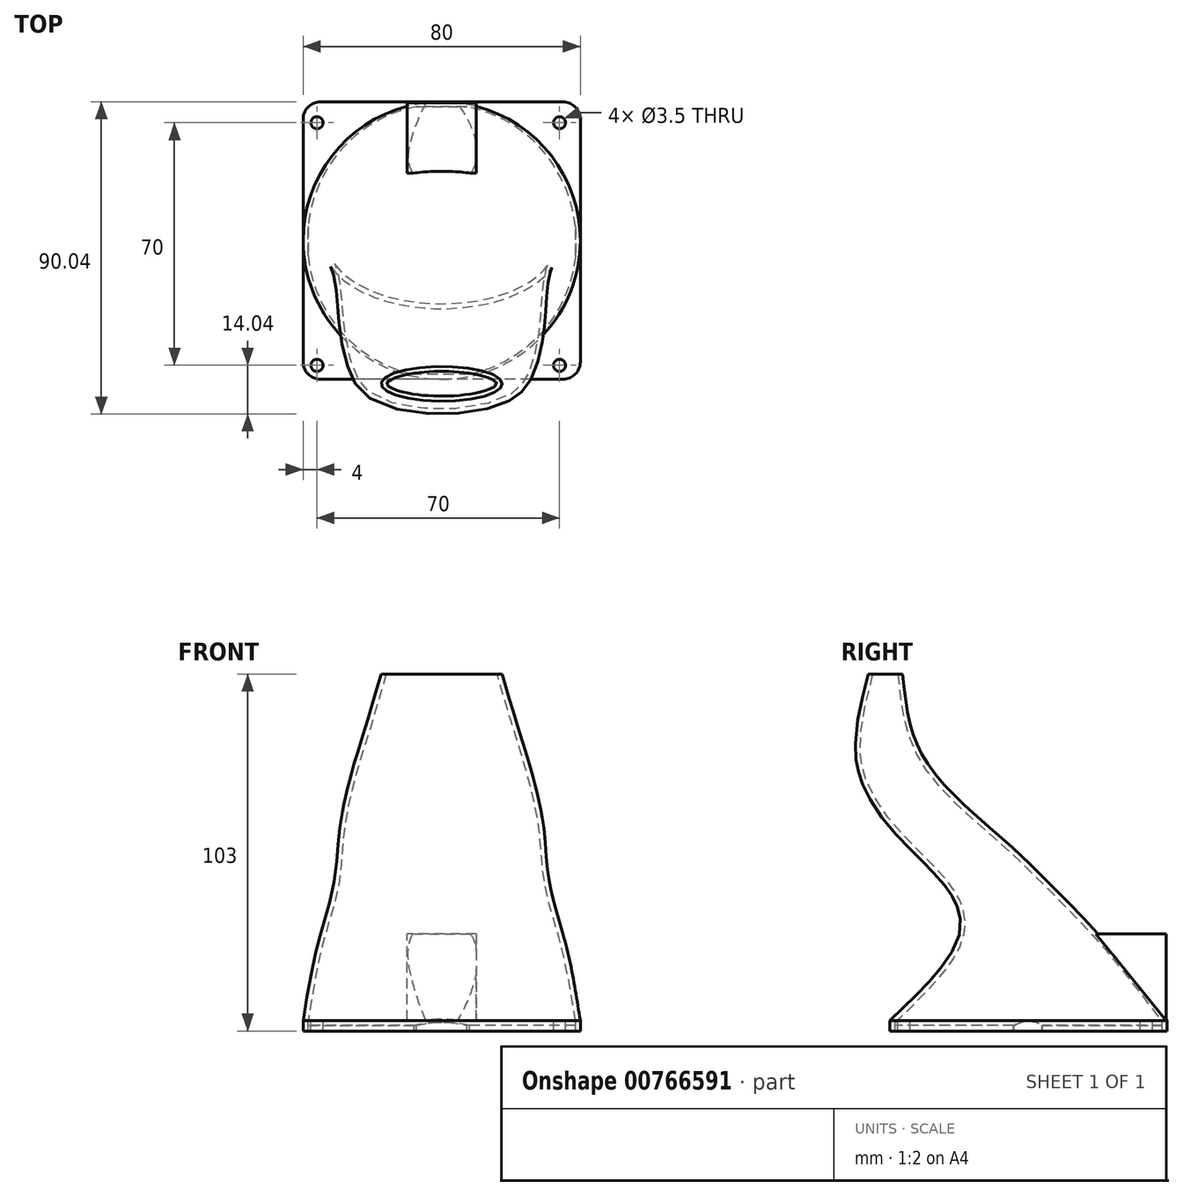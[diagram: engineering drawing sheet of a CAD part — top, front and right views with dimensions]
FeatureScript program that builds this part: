
annotation { "Feature Type Name" : "Feature", "Feature Type Description" : "" }
export const myFeature = defineFeature(function(context is Context, id is Id, definition is map)
    precondition{}
    {
        {
            var Q0;
            Q0=qCreatedBy(makeId("Top.planeOp"),FACE);
            var sketch = newSketch(context, id + "F0", { "sketchPlane" : qUnion([Q0])});
            skEllipse(sketch, "E0", {"center": v(0, 0) * mm, "majorRadius": 35 * mm, "minorRadius": 20 * mm, "majorAxis": v(1, 0)});
            skSolve(sketch);
        }
        {
            var Q0;
            Q0=qCreatedBy(makeId("Top.planeOp"),FACE);
            cPlane(context, id + "F1", {"entities" : qUnion([Q0]), "cplaneType" : CPlaneType.OFFSET, "offset" : 25 * mm, "oppositeDirection" : true, "width" : 150 * mm, "height" : 150 * mm});
        }
        {
            var Q0;
            Q0=qCreatedBy(id+"F1.planeOp",FACE);
            var sketch = newSketch(context, id + "F2", { "sketchPlane" : qUnion([Q0])});
            skCircle(sketch, "E1", {"center": v(0, 0) * mm, "radius": 40 * mm});
            skSolve(sketch);
        }
        {
            var Q0;
            Q0=qCreatedBy(makeId("Top.planeOp"),FACE);
            cPlane(context, id + "F3", {"entities" : qUnion([Q0]), "cplaneType" : CPlaneType.OFFSET, "offset" : 25 * mm, "width" : 150 * mm, "height" : 150 * mm});
        }
        {
            var Q0;
            Q0=qCreatedBy(id+"F3.planeOp",FACE);
            var sketch = newSketch(context, id + "F4", { "sketchPlane" : qUnion([Q0])});
            skEllipse(sketch, "E2", {"center": v(0, -19.77) * mm, "majorRadius": 30 * mm, "minorRadius": 15 * mm, "majorAxis": v(1, 0)});
            skSolve(sketch);
        }
        {
            var Q0;
            Q0=qCreatedBy(id+"F3.planeOp",FACE);
            cPlane(context, id + "F5", {"entities" : qUnion([Q0]), "cplaneType" : CPlaneType.OFFSET, "offset" : 25 * mm, "width" : 150 * mm, "height" : 150 * mm});
        }
        {
            var Q0;
            Q0=qCreatedBy(id+"F5.planeOp",FACE);
            var sketch = newSketch(context, id + "F6", { "sketchPlane" : qUnion([Q0])});
            skEllipse(sketch, "E3", {"center": v(0, -39.76) * mm, "majorRadius": 25 * mm, "minorRadius": 10 * mm, "majorAxis": v(1, 0)});
            skSolve(sketch);
        }
        {
            var Q0;
            Q0=qCreatedBy(id+"F5.planeOp",FACE);
            cPlane(context, id + "F7", {"entities" : qUnion([Q0]), "cplaneType" : CPlaneType.OFFSET, "offset" : 25 * mm, "width" : 150 * mm, "height" : 150 * mm});
        }
        {
            var Q0;
            Q0=qCreatedBy(id+"F7.planeOp",FACE);
            var sketch = newSketch(context, id + "F8", { "sketchPlane" : qUnion([Q0])});
            skEllipse(sketch, "E4", {"center": v(0, -41.33) * mm, "majorRadius": 17.5 * mm, "minorRadius": 5 * mm, "majorAxis": v(1, 0)});
            skSolve(sketch);
        }
        {
            var Q0;
            Q0=makeQuery(id+"F2.imprint","IMPRINT",FACE,{"disambiguationData":[TD([[makeQuery(id+"F2.imprint","IMPRINT",EDGE,{"derivedFrom":sQuery(id+"F2.wireOp",EDGE,"E1")}),1.0]])]});
            var Q1;
            Q1=makeQuery(id+"F0.imprint","IMPRINT",FACE,{"disambiguationData":[TD([[makeQuery(id+"F0.imprint","IMPRINT",EDGE,{"derivedFrom":sQuery(id+"F0.wireOp",EDGE,"E0")}),1.0]])]});
            var Q2;
            Q2=makeQuery(id+"F4.imprint","IMPRINT",FACE,{"disambiguationData":[TD([[makeQuery(id+"F4.imprint","IMPRINT",EDGE,{"derivedFrom":sQuery(id+"F4.wireOp",EDGE,"E2")}),1.0]])]});
            var Q3;
            Q3=makeQuery(id+"F6.imprint","IMPRINT",FACE,{"disambiguationData":[TD([[makeQuery(id+"F6.imprint","IMPRINT",EDGE,{"derivedFrom":sQuery(id+"F6.wireOp",EDGE,"E3")}),1.0]])]});
            var Q4;
            Q4=makeQuery(id+"F8.imprint","IMPRINT",FACE,{"disambiguationData":[TD([[makeQuery(id+"F8.imprint","IMPRINT",EDGE,{"derivedFrom":sQuery(id+"F8.wireOp",EDGE,"E4")}),1.0]])]});
            loft(context, id + "F9", {"sheetProfilesArray" : [{ "sheetProfileEntities" : qUnion([Q0]) }, { "sheetProfileEntities" : qUnion([Q1]) }, { "sheetProfileEntities" : qUnion([Q2]) }, { "sheetProfileEntities" : qUnion([Q3]) }, { "sheetProfileEntities" : qUnion([Q4]) }]});
        }
        {
            var Q0;
            Q0=makeQuery(id+"F9.opLoft","CAP_FACE",FACE,{"disambiguationData":[OSD([makeQuery(id+"F2.imprint","IMPRINT",FACE,{"disambiguationData":[TD([[makeQuery(id+"F2.imprint","IMPRINT",EDGE,{"derivedFrom":sQuery(id+"F2.wireOp",EDGE,"E1")}),1.0]])]})])],"isStart":true});
            var sketch = newSketch(context, id + "F10", { "sketchPlane" : qUnion([Q0])});
            skLineSegment(sketch, "E5.bottom", {"start": v(40, -40) * mm, "end": v(-40, -40) * mm});
            skLineSegment(sketch, "E5.top", {"start": v(40, 40) * mm, "end": v(-40, 40) * mm});
            skLineSegment(sketch, "E5.left", {"start": v(40, -40) * mm, "end": v(40, 40) * mm});
            skLineSegment(sketch, "E5.right", {"start": v(-40, -40) * mm, "end": v(-40, 40) * mm});
            skCircle(sketch, "E6", {"center": v(34, -34) * mm, "radius": 1.75 * mm});
            skCircle(sketch, "E7.0.1.0", {"center": v(34, 36) * mm, "radius": 1.75 * mm});
            skCircle(sketch, "E7.1.0.0", {"center": v(-36, -34) * mm, "radius": 1.75 * mm});
            skCircle(sketch, "E7.1.1.0", {"center": v(-36, 36) * mm, "radius": 1.75 * mm});
            skLineSegment(sketch, "E7.direction1", {"start": v(34, -34) * mm, "end": v(-36, -34) * mm, "construction": true});
            skLineSegment(sketch, "E7.direction2", {"start": v(34, -34) * mm, "end": v(34, 36) * mm, "construction": true});
            skSolve(sketch);
        }
        {
            var Q0;
            {var subQ0=sQuery(id+"F10.wireOp",EDGE,"E5.left");var subQ1=sQuery(id+"F10.wireOp",EDGE,"E5.bottom");var subQ2=makeQuery(id+"F10.imprint","INTERSECT",VERTEX,{"derivedFrom":[subQ1,subQ0]});Q0=makeQuery(id+"F10.imprint","IMPRINT",FACE,{"disambiguationData":[TD([[makeQuery(id+"F10.imprint","IMPRINT",EDGE,{"disambiguationData":[TD([[subQ2,-1.0]])],"derivedFrom":subQ1}),-1.0]])]});}
            var Q1;
            {var subQ0=makeQuery(id+"F9.opLoft","MID_CAP_EDGE",EDGE,{"disambiguationData":[OSD([sQuery(id+"F2.wireOp",EDGE,"E1")])],"capPos":0.0});var subQ1=makeQuery(id+"F10.imprint","INTERSECT",VERTEX,{"derivedFrom":[subQ0,sQuery(id+"F10.wireOp",EDGE,"E5.bottom")]});Q1=makeQuery(id+"F10.imprint","IMPRINT",FACE,{"disambiguationData":[TD([[makeQuery(id+"F10.imprint","IMPRINT",EDGE,{"disambiguationData":[TD([[subQ1,-1.0]])],"derivedFrom":subQ0}),1.0]])]});}
            var Q2;
            {var subQ0=sQuery(id+"F10.wireOp",EDGE,"E5.right");var subQ1=sQuery(id+"F10.wireOp",EDGE,"E5.bottom");var subQ2=makeQuery(id+"F10.imprint","INTERSECT",VERTEX,{"derivedFrom":[subQ1,subQ0]});Q2=makeQuery(id+"F10.imprint","IMPRINT",FACE,{"disambiguationData":[TD([[makeQuery(id+"F10.imprint","IMPRINT",EDGE,{"disambiguationData":[TD([[subQ2,1.0]])],"derivedFrom":subQ1}),-1.0]])]});}
            var Q3;
            {var subQ0=sQuery(id+"F10.wireOp",EDGE,"E5.right");var subQ1=sQuery(id+"F10.wireOp",EDGE,"E5.top");var subQ2=makeQuery(id+"F10.imprint","INTERSECT",VERTEX,{"derivedFrom":[subQ1,subQ0]});Q3=makeQuery(id+"F10.imprint","IMPRINT",FACE,{"disambiguationData":[TD([[makeQuery(id+"F10.imprint","IMPRINT",EDGE,{"disambiguationData":[TD([[subQ2,1.0]])],"derivedFrom":subQ1}),1.0]])]});}
            var Q4;
            {var subQ0=sQuery(id+"F10.wireOp",EDGE,"E5.left");var subQ1=sQuery(id+"F10.wireOp",EDGE,"E5.top");var subQ2=makeQuery(id+"F10.imprint","INTERSECT",VERTEX,{"derivedFrom":[subQ1,subQ0]});Q4=makeQuery(id+"F10.imprint","IMPRINT",FACE,{"disambiguationData":[TD([[makeQuery(id+"F10.imprint","IMPRINT",EDGE,{"disambiguationData":[TD([[subQ2,-1.0]])],"derivedFrom":subQ1}),1.0]])]});}
            extrude(context, id + "F11", {"entities" : qUnion([Q0, Q1, Q2, Q3, Q4]), "operationType" : NewBodyOperationType.ADD, "depth" : 3 * mm, "offsetDistance" : 25 * mm});
        }
        {
            var Q0;
            Q0=makeQuery(id+"F9.opLoft","CAP_FACE",FACE,{"disambiguationData":[OSD([makeQuery(id+"F8.imprint","IMPRINT",FACE,{"disambiguationData":[TD([[makeQuery(id+"F8.imprint","IMPRINT",EDGE,{"derivedFrom":sQuery(id+"F8.wireOp",EDGE,"E4")}),1.0]])]})])],"isStart":true});
            var Q1;
            Q1=makeQuery(id+"F11.opExtrude","CAP_FACE",FACE,{"disambiguationData":[OSD([sQuery(id+"F10.wireOp",EDGE,"E5.bottom"),sQuery(id+"F10.wireOp",EDGE,"E5.top"),sQuery(id+"F10.wireOp",EDGE,"E5.left"),sQuery(id+"F10.wireOp",EDGE,"E5.right"),sQuery(id+"F10.wireOp",EDGE,"E6"),sQuery(id+"F10.wireOp",EDGE,"E7.0.1.0"),sQuery(id+"F10.wireOp",EDGE,"E7.1.0.0"),sQuery(id+"F10.wireOp",EDGE,"E7.1.1.0")])],"isStart":false});
            shell(context, id + "F12", {"entities" : qUnion([Q0, Q1]), "thickness" : 1.4 * mm});
        }
        {
            var Q0;
            {var subQ0=sQuery(id+"F10.wireOp",EDGE,"E5.left");var subQ1=sQuery(id+"F10.wireOp",EDGE,"E7.1.1.0");var subQ2=sQuery(id+"F10.wireOp",EDGE,"E7.1.0.0");var subQ3=sQuery(id+"F10.wireOp",EDGE,"E7.0.1.0");var subQ4=sQuery(id+"F10.wireOp",EDGE,"E6");var subQ5=sQuery(id+"F10.wireOp",EDGE,"E5.right");var subQ6=sQuery(id+"F10.wireOp",EDGE,"E5.top");var subQ7=sQuery(id+"F10.wireOp",EDGE,"E5.bottom");var subQ8=makeQuery(id+"F11.opExtrude","CAP_FACE",FACE,{"disambiguationData":[OSD([subQ7,subQ6,subQ0,subQ5,subQ4,subQ3,subQ2,subQ1])],"isStart":true});Q0=makeQuery(id+"F12.opShell","OFFSET_FACE",FACE,{"disambiguationData":[OSD([subQ7,subQ6,subQ0,subQ5,subQ4,subQ3,subQ2,subQ1]),TDD([makeQuery(id+"F11.boolean.opBoolean","SPLIT",FACE,{"disambiguationData":[TD([makeQuery(id+"F11.opExtrude","SWEPT_FACE",FACE,{"disambiguationData":[OSD([subQ4])]})])],"derivedFrom":subQ8})])]});}
            var Q1;
            {var subQ0=sQuery(id+"F10.wireOp",EDGE,"E7.1.1.0");var subQ1=sQuery(id+"F10.wireOp",EDGE,"E7.1.0.0");var subQ2=sQuery(id+"F10.wireOp",EDGE,"E7.0.1.0");var subQ3=sQuery(id+"F10.wireOp",EDGE,"E6");var subQ4=sQuery(id+"F10.wireOp",EDGE,"E5.right");var subQ5=sQuery(id+"F10.wireOp",EDGE,"E5.left");var subQ6=sQuery(id+"F10.wireOp",EDGE,"E5.top");var subQ7=sQuery(id+"F10.wireOp",EDGE,"E5.bottom");var subQ8=makeQuery(id+"F11.opExtrude","CAP_FACE",FACE,{"disambiguationData":[OSD([subQ7,subQ6,subQ5,subQ4,subQ3,subQ2,subQ1,subQ0])],"isStart":true});Q1=makeQuery(id+"F12.opShell","OFFSET_FACE",FACE,{"disambiguationData":[OSD([subQ7,subQ6,subQ5,subQ4,subQ3,subQ2,subQ1,subQ0]),TDD([makeQuery(id+"F11.boolean.opBoolean","SPLIT",FACE,{"disambiguationData":[TD([makeQuery(id+"F11.opExtrude","SWEPT_FACE",FACE,{"disambiguationData":[OSD([subQ1])]})])],"derivedFrom":subQ8})])]});}
            var Q2;
            {var subQ0=sQuery(id+"F10.wireOp",EDGE,"E5.right");var subQ1=sQuery(id+"F10.wireOp",EDGE,"E5.top");var subQ2=sQuery(id+"F10.wireOp",EDGE,"E7.1.1.0");var subQ3=sQuery(id+"F10.wireOp",EDGE,"E7.1.0.0");var subQ4=sQuery(id+"F10.wireOp",EDGE,"E7.0.1.0");var subQ5=sQuery(id+"F10.wireOp",EDGE,"E6");var subQ6=sQuery(id+"F10.wireOp",EDGE,"E5.left");var subQ7=sQuery(id+"F10.wireOp",EDGE,"E5.bottom");var subQ8=makeQuery(id+"F11.opExtrude","CAP_FACE",FACE,{"disambiguationData":[OSD([subQ7,subQ1,subQ6,subQ0,subQ5,subQ4,subQ3,subQ2])],"isStart":true});Q2=makeQuery(id+"F12.opShell","OFFSET_FACE",FACE,{"disambiguationData":[OSD([subQ7,subQ1,subQ6,subQ0,subQ5,subQ4,subQ3,subQ2]),TDD([makeQuery(id+"F11.boolean.opBoolean","SPLIT",FACE,{"disambiguationData":[TD([makeQuery(id+"F11.opExtrude","SWEPT_FACE",FACE,{"disambiguationData":[OSD([subQ2])]})])],"derivedFrom":subQ8})]),OD(1.0)]});}
            var Q3;
            {var subQ0=sQuery(id+"F10.wireOp",EDGE,"E5.left");var subQ1=sQuery(id+"F10.wireOp",EDGE,"E5.top");var subQ2=sQuery(id+"F10.wireOp",EDGE,"E7.1.1.0");var subQ3=sQuery(id+"F10.wireOp",EDGE,"E7.1.0.0");var subQ4=sQuery(id+"F10.wireOp",EDGE,"E7.0.1.0");var subQ5=sQuery(id+"F10.wireOp",EDGE,"E6");var subQ6=sQuery(id+"F10.wireOp",EDGE,"E5.right");var subQ7=sQuery(id+"F10.wireOp",EDGE,"E5.bottom");var subQ8=makeQuery(id+"F11.opExtrude","CAP_FACE",FACE,{"disambiguationData":[OSD([subQ7,subQ1,subQ0,subQ6,subQ5,subQ4,subQ3,subQ2])],"isStart":true});Q3=makeQuery(id+"F12.opShell","OFFSET_FACE",FACE,{"disambiguationData":[OSD([subQ7,subQ1,subQ0,subQ6,subQ5,subQ4,subQ3,subQ2]),TDD([makeQuery(id+"F11.boolean.opBoolean","SPLIT",FACE,{"disambiguationData":[TD([makeQuery(id+"F11.opExtrude","SWEPT_FACE",FACE,{"disambiguationData":[OSD([subQ4])]})])],"derivedFrom":subQ8})])]});}
            var Q4;
            {var subQ0=sQuery(id+"F10.wireOp",EDGE,"E5.right");var subQ1=sQuery(id+"F10.wireOp",EDGE,"E5.top");var subQ2=sQuery(id+"F10.wireOp",EDGE,"E7.1.1.0");var subQ3=sQuery(id+"F10.wireOp",EDGE,"E7.1.0.0");var subQ4=sQuery(id+"F10.wireOp",EDGE,"E7.0.1.0");var subQ5=sQuery(id+"F10.wireOp",EDGE,"E6");var subQ6=sQuery(id+"F10.wireOp",EDGE,"E5.left");var subQ7=sQuery(id+"F10.wireOp",EDGE,"E5.bottom");var subQ8=makeQuery(id+"F11.opExtrude","CAP_FACE",FACE,{"disambiguationData":[OSD([subQ7,subQ1,subQ6,subQ0,subQ5,subQ4,subQ3,subQ2])],"isStart":true});Q4=makeQuery(id+"F12.opShell","OFFSET_FACE",FACE,{"disambiguationData":[OSD([subQ7,subQ1,subQ6,subQ0,subQ5,subQ4,subQ3,subQ2]),TDD([makeQuery(id+"F11.boolean.opBoolean","SPLIT",FACE,{"disambiguationData":[TD([makeQuery(id+"F11.opExtrude","SWEPT_FACE",FACE,{"disambiguationData":[OSD([subQ2])]})])],"derivedFrom":subQ8})]),OD(0.0)]});}
            extrude(context, id + "F13", {"entities" : qUnion([Q0, Q1, Q2, Q3, Q4]), "operationType" : NewBodyOperationType.ADD, "depth" : 1.6 * mm, "offsetDistance" : 25 * mm});
        }
        {
            var Q0;
            Q0=qCreatedBy(makeId("Right.planeOp"),FACE);
            var sketch = newSketch(context, id + "F14", { "sketchPlane" : qUnion([Q0])});
            skLineSegment(sketch, "E8", {"start": v(39.7, -24.95) * mm, "end": v(19.42, 0) * mm});
            skLineSegment(sketch, "E9", {"start": v(19.42, 0) * mm, "end": v(39.7, 0) * mm});
            skLineSegment(sketch, "E10", {"start": v(39.7, 0) * mm, "end": v(39.7, -24.95) * mm});
            skSolve(sketch);
        }
        {
            var Q0;
            Q0=makeQuery(id+"F14.imprint","IMPRINT",FACE,{"disambiguationData":[TD([[makeQuery(id+"F14.imprint","IMPRINT",EDGE,{"derivedFrom":sQuery(id+"F14.wireOp",EDGE,"E8")}),-1.0]])]});
            extrude(context, id + "F15", {"entities" : qUnion([Q0]), "operationType" : NewBodyOperationType.ADD, "depth" : 10 * mm, "offsetDistance" : 25 * mm, "hasSecondDirection" : true, "secondDirectionOppositeDirection" : true, "secondDirectionDepth" : 10 * mm});
        }
        {
            var Q0;
            Q0=makeQuery(id+"F11.opExtrude","SWEPT_EDGE",EDGE,{"disambiguationData":[OSD([sQuery(id+"F10.wireOp",EDGE,"E5.bottom"),sQuery(id+"F10.wireOp",EDGE,"E5.right")])]});
            var Q1;
            Q1=makeQuery(id+"F11.opExtrude","SWEPT_EDGE",EDGE,{"disambiguationData":[OSD([sQuery(id+"F10.wireOp",EDGE,"E5.top"),sQuery(id+"F10.wireOp",EDGE,"E5.right")])]});
            var Q2;
            Q2=makeQuery(id+"F11.opExtrude","SWEPT_EDGE",EDGE,{"disambiguationData":[OSD([sQuery(id+"F10.wireOp",EDGE,"E5.top"),sQuery(id+"F10.wireOp",EDGE,"E5.left")])]});
            var Q3;
            Q3=makeQuery(id+"F11.opExtrude","SWEPT_EDGE",EDGE,{"disambiguationData":[OSD([sQuery(id+"F10.wireOp",EDGE,"E5.bottom"),sQuery(id+"F10.wireOp",EDGE,"E5.left")])]});
            fillet(context, id + "F16", {"entities" : qUnion([Q0, Q1, Q2, Q3]), "radius" : 5 * mm, "tangentPropagation" : true, "allowEdgeOverflow" : false});
        }
    });
